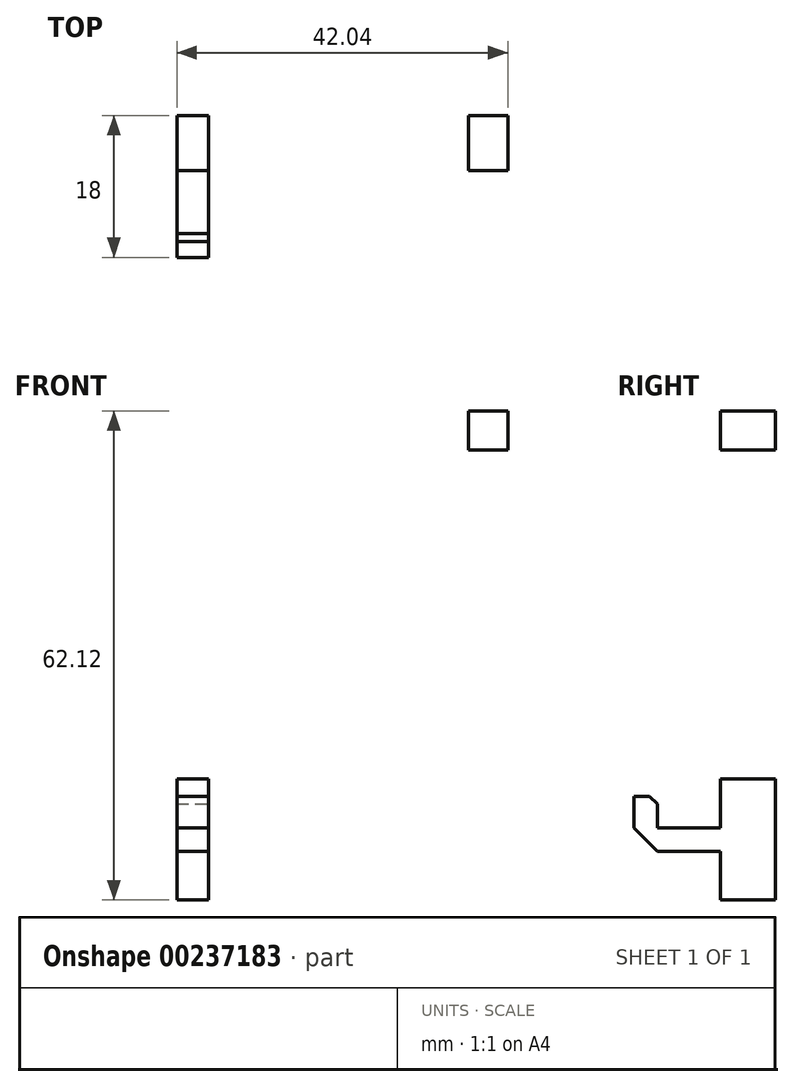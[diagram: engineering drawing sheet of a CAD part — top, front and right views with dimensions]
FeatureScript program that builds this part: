
annotation { "Feature Type Name" : "Feature", "Feature Type Description" : "" }
export const myFeature = defineFeature(function(context is Context, id is Id, definition is map)
    precondition{}
    {
        {
            assignVariable(context, id + "F0", {"name" : "standoff_height", "anyValue" : 7});
        }
        {
            var Q0;
            Q0=qCreatedBy(makeId("Front.planeOp"),FACE);
            var sketch = newSketch(context, id + "F1", { "sketchPlane" : qUnion([Q0])});
            skLineSegment(sketch, "E0.bottom", {"start": v(-44.9, 54.45) * mm, "end": v(-49.9, 54.45) * mm});
            skLineSegment(sketch, "E0.top", {"start": v(-44.9, 49.45) * mm, "end": v(-49.9, 49.45) * mm});
            skLineSegment(sketch, "E0.left", {"start": v(-44.9, 54.45) * mm, "end": v(-44.9, 49.45) * mm});
            skLineSegment(sketch, "E0.right", {"start": v(-49.9, 54.45) * mm, "end": v(-49.9, 49.45) * mm});
            skPoint(sketch, "E0.middle", {"position": v(-47.4, 51.95) * mm});
            skPoint(sketch, "E0.middle.positionSnap0", {"position": v(-47.4, 59.75) * mm});
            skPoint(sketch, "E0.centerSnap0", {"position": v(-47.4, 59.75) * mm});
            skLineSegment(sketch, "E1.bottom", {"start": v(-44.9, -49.66) * mm, "end": v(-49.9, -49.66) * mm});
            skLineSegment(sketch, "E1.top", {"start": v(-44.9, -54.66) * mm, "end": v(-49.9, -54.66) * mm});
            skLineSegment(sketch, "E1.left", {"start": v(-44.9, -49.66) * mm, "end": v(-44.9, -54.66) * mm});
            skLineSegment(sketch, "E1.right", {"start": v(-49.9, -49.66) * mm, "end": v(-49.9, -54.66) * mm});
            skPoint(sketch, "E1.middle", {"position": v(-47.4, -52.16) * mm});
            skPoint(sketch, "E1.middle.positionSnap0", {"position": v(-47.4, -59.75) * mm});
            skPoint(sketch, "E1.centerSnap0", {"position": v(-47.4, -59.75) * mm});
            skSolve(sketch);
        }
        {
            var Q0;
            Q0=makeQuery(id+"F1.imprint","IMPRINT",FACE,{"disambiguationData":[TD([[makeQuery(id+"F1.imprint","IMPRINT",EDGE,{"derivedFrom":sQuery(id+"F1.wireOp",EDGE,"E0.bottom")}),1.0]])]});
            extrude(context, id + "F2", {"entities" : qUnion([Q0]), "depth" : (getVariable(context, 'standoff_height')) * mm});
        }
        {
            assignVariable(context, id + "F3", {"name" : "pegboard_depth", "anyValue" : 8});
        }
        {
            assignVariable(context, id + "F4", {"name" : "peg_diameter", "anyValue" : 3});
        }
        {
            var Q0;
            Q0=qCreatedBy(makeId("Front.planeOp"),FACE);
            var sketch = newSketch(context, id + "F5", { "sketchPlane" : qUnion([Q0])});
            skLineSegment(sketch, "E2.bottom", {"start": v(-82.94, -7.67) * mm, "end": v(-86.94, -7.67) * mm});
            skLineSegment(sketch, "E2.top", {"start": v(-82.94, 7.67) * mm, "end": v(-86.94, 7.67) * mm});
            skLineSegment(sketch, "E2.left", {"start": v(-82.94, -7.67) * mm, "end": v(-82.94, 7.67) * mm});
            skLineSegment(sketch, "E2.right", {"start": v(-86.94, -7.67) * mm, "end": v(-86.94, 7.67) * mm});
            skPoint(sketch, "E2.middle", {"position": v(-84.94, 0) * mm});
            skLineSegment(sketch, "E3.bottom", {"start": v(77.06, 7.67) * mm, "end": v(87.06, 7.67) * mm});
            skLineSegment(sketch, "E3.top", {"start": v(77.06, -7.67) * mm, "end": v(87.06, -7.67) * mm});
            skLineSegment(sketch, "E3.left", {"start": v(77.06, 7.67) * mm, "end": v(77.06, -7.67) * mm});
            skLineSegment(sketch, "E3.right", {"start": v(87.06, 7.67) * mm, "end": v(87.06, -7.67) * mm});
            skPoint(sketch, "E3.middle", {"position": v(82.06, 0) * mm});
            skPoint(sketch, "E3.centerSnap0", {"position": v(97.5, 0) * mm});
            skSolve(sketch);
        }
        {
            var Q0;
            Q0=makeQuery(id+"F5.imprint","IMPRINT",FACE,{"disambiguationData":[TD([[makeQuery(id+"F5.imprint","IMPRINT",EDGE,{"derivedFrom":sQuery(id+"F5.wireOp",EDGE,"E2.bottom")}),1.0]])]});
            var Q1;
            Q1=makeQuery(id+"F5.imprint","IMPRINT",FACE,{"disambiguationData":[TD([[makeQuery(id+"F5.imprint","IMPRINT",EDGE,{"derivedFrom":sQuery(id+"F5.wireOp",EDGE,"E2.bottom")}),-1.0]])]});
            extrude(context, id + "F6", {"entities" : qUnion([Q0, Q1]), "depth" : (getVariable(context, 'standoff_height')) * mm});
        }
        {
            var Q0;
            Q0=makeQuery(id+"F6.opExtrude","CAP_FACE",FACE,{"disambiguationData":[OSD([sQuery(id+"F5.wireOp",EDGE,"E2.bottom"),sQuery(id+"F5.wireOp",EDGE,"E2.top"),sQuery(id+"F5.wireOp",EDGE,"E2.left"),sQuery(id+"F5.wireOp",EDGE,"E2.right")])],"isStart":false});
            var sketch = newSketch(context, id + "F7", { "sketchPlane" : qUnion([Q0])});
            skPoint(sketch, "E4.centerSnap0", {"position": v(-84.94, 7.67) * mm});
            skLineSegment(sketch, "E5.bottom", {"start": v(-82.94, -1.5) * mm, "end": v(-86.94, -1.5) * mm});
            skLineSegment(sketch, "E5.top", {"start": v(-82.94, 1.5) * mm, "end": v(-86.94, 1.5) * mm});
            skLineSegment(sketch, "E5.left", {"start": v(-82.94, -1.5) * mm, "end": v(-82.94, 1.5) * mm});
            skLineSegment(sketch, "E5.right", {"start": v(-86.94, -1.5) * mm, "end": v(-86.94, 1.5) * mm});
            skPoint(sketch, "E5.middle", {"position": v(-84.94, 0) * mm});
            skSolve(sketch);
        }
        {
            var Q0;
            Q0=makeQuery(id+"F7.imprint","IMPRINT",FACE,{"disambiguationData":[TD([[makeQuery(id+"F7.imprint","IMPRINT",EDGE,{"derivedFrom":sQuery(id+"F7.wireOp",EDGE,"E5.bottom")}),-1.0]])]});
            extrude(context, id + "F8", {"entities" : qUnion([Q0]), "operationType" : NewBodyOperationType.ADD, "depth" : (getVariable(context, 'pegboard_depth') + getVariable(context, 'peg_diameter')) * mm});
        }
        {
            var Q0;
            Q0=makeQuery(id+"F8.opExtrude","SWEPT_FACE",FACE,{"disambiguationData":[OSD([sQuery(id+"F7.wireOp",EDGE,"E5.top")])]});
            var sketch = newSketch(context, id + "F9", { "sketchPlane" : qUnion([Q0])});
            skLineSegment(sketch, "E6", {"start": v(-86.94, -15) * mm, "end": v(-82.94, -15) * mm});
            skLineSegment(sketch, "E7.left", {"start": v(-82.94, -15) * mm, "end": v(-82.94, -15) * mm});
            skLineSegment(sketch, "E7.right", {"start": v(-86.94, -18) * mm, "end": v(-86.94, -18) * mm});
            skSolve(sketch);
        }
        {
            var Q0;
            {var subQ0=sQuery(id+"F9.wireOp",EDGE,"E6");Q0=makeQuery(id+"F9.imprint","IMPRINT",FACE,{"disambiguationData":[TD([[makeQuery(id+"F9.imprint","IMPRINT",EDGE,{"derivedFrom":subQ0}),-1.0]])]});}
            extrude(context, id + "F10", {"entities" : qUnion([Q0]), "operationType" : NewBodyOperationType.ADD, "depth" : (getVariable(context, 'pegboard_depth') / 2) * mm});
        }
        {
            var Q0;
            Q0=makeQuery(id+"F8.opExtrude","CAP_EDGE",EDGE,{"disambiguationData":[OSD([sQuery(id+"F7.wireOp",EDGE,"E5.bottom")])],"isStart":false});
            chamfer(context, id + "F11", {"entities" : qUnion([Q0]), "width" : 3 * mm, "tangentPropagation" : true});
        }
        {
            var Q0;
            Q0=makeQuery(id+"F10.opExtrude","CAP_EDGE",EDGE,{"disambiguationData":[OSD([sQuery(id+"F9.wireOp",EDGE,"E6")])],"isStart":false});
            chamfer(context, id + "F12", {"entities" : qUnion([Q0]), "width" : 1 * mm, "tangentPropagation" : true});
        }
    });
